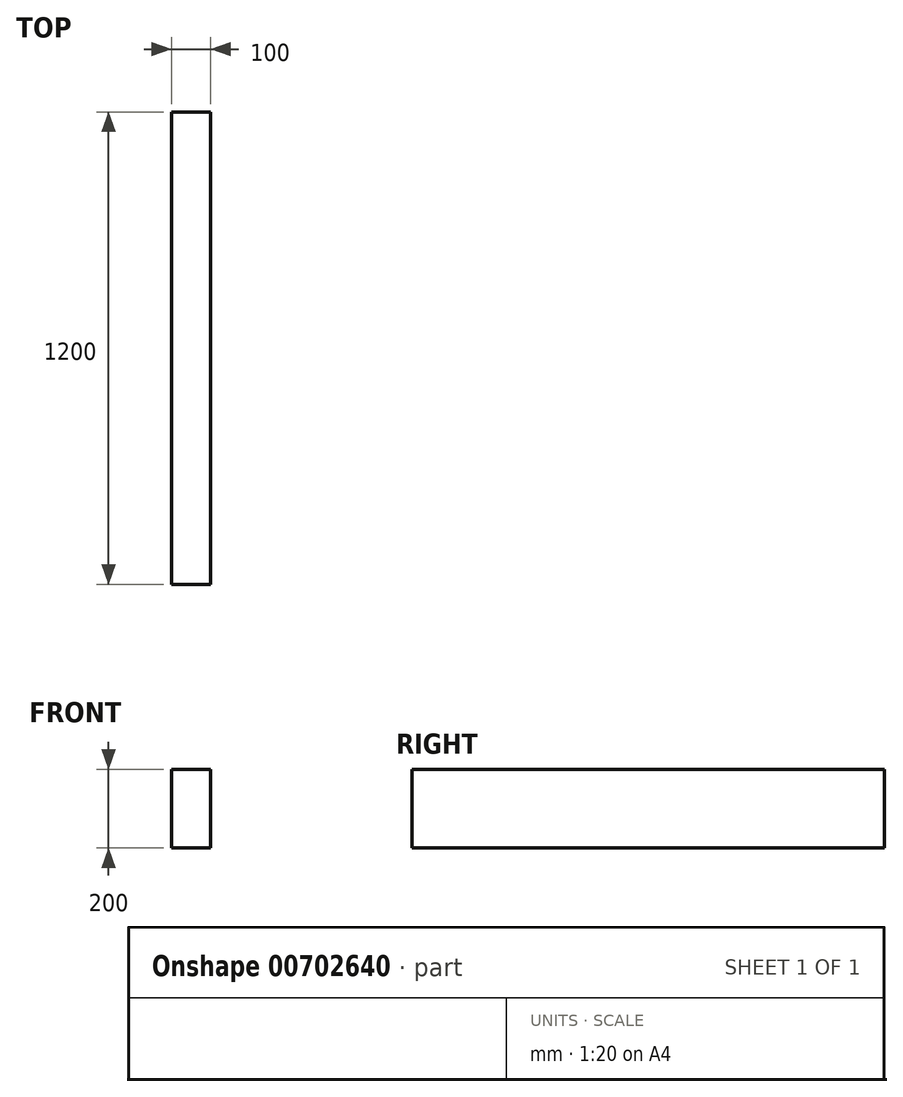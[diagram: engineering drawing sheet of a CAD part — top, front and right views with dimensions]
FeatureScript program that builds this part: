
annotation { "Feature Type Name" : "Feature", "Feature Type Description" : "" }
export const myFeature = defineFeature(function(context is Context, id is Id, definition is map)
    precondition{}
    {
        {
            var Q0;
            Q0=qCreatedBy(makeId("Front.planeOp"),FACE);
            var sketch = newSketch(context, id + "F0", { "sketchPlane" : qUnion([Q0])});
            skLineSegment(sketch, "E0.bottom", {"start": v(0, 0) * mm, "end": v(-100, 0) * mm});
            skLineSegment(sketch, "E0.top", {"start": v(0, 200) * mm, "end": v(-100, 200) * mm});
            skLineSegment(sketch, "E0.left", {"start": v(0, 0) * mm, "end": v(0, 200) * mm});
            skLineSegment(sketch, "E0.right", {"start": v(-100, 0) * mm, "end": v(-100, 200) * mm});
            skSolve(sketch);
        }
        {
            var Q0;
            Q0=qSketchRegion(id+"F0",true);
            extrude(context, id + "F1", {"entities" : qUnion([Q0]), "depth" : 1200 * mm, "offsetDistance" : 25 * mm});
        }
    });
